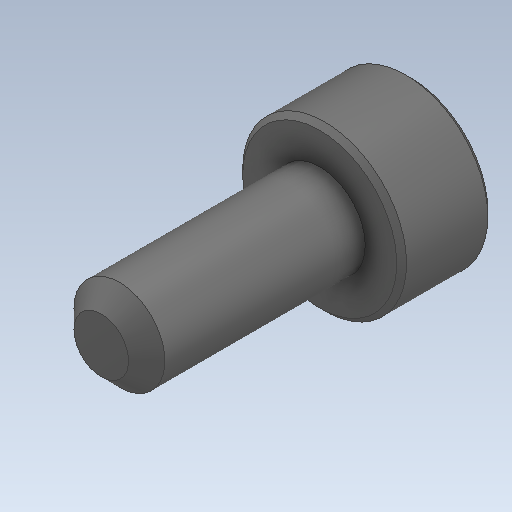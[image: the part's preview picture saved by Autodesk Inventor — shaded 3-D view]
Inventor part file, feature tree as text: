
AUTODESK INVENTOR PART (.ipt)
format: ipt  version: 2020 (Build 240168000, 168)  size: 134,144 bytes
history: native  units: in
note: dims shown in document units (in); Inventor stores cm internally (conversion verified against a paired STEP export)
features: chamfer x1
ambient origin geometry x8: Origin, YZ Plane, XZ Plane, XY Plane, X Axis, Y Axis, Z Axis, Center Point
bodies: Solid1 (feature_tree)
feature tree (1):
  chamfer  "Chamfer2"  [1 undecoded]
note: 1 required parameter value undecoded (feature->parameter linkage not recoverable at this tier; creation-order binding heuristic only, values carry confidence <= 0.55)
